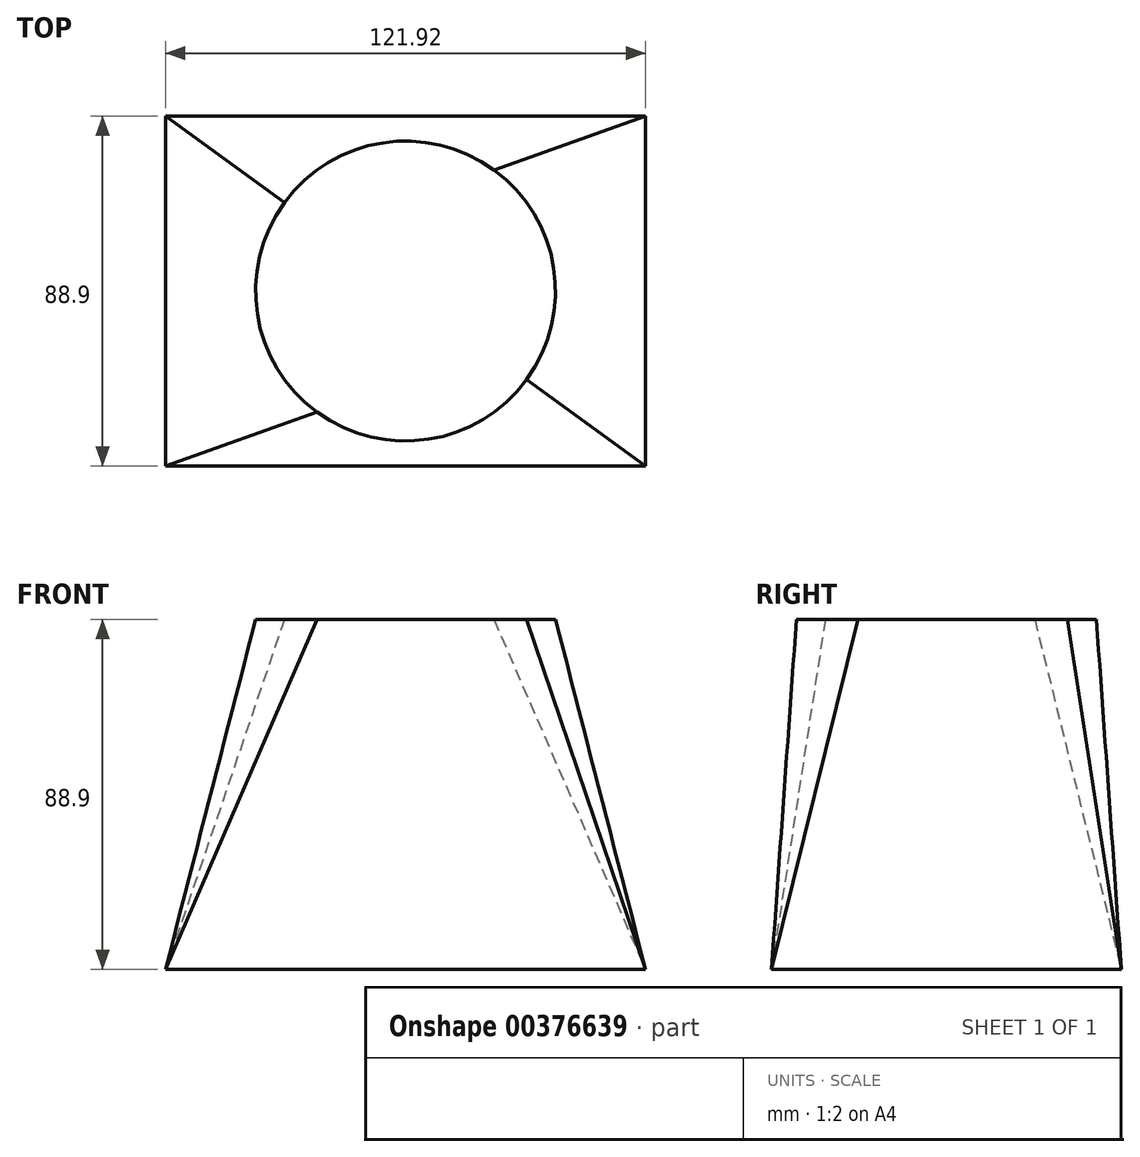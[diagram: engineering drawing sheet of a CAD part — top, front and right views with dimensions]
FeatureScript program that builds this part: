
annotation { "Feature Type Name" : "Feature", "Feature Type Description" : "" }
export const myFeature = defineFeature(function(context is Context, id is Id, definition is map)
    precondition{}
    {
        {
            var Q0;
            Q0=qCreatedBy(makeId("Top.planeOp"),FACE);
            var sketch = newSketch(context, id + "F0", { "sketchPlane" : qUnion([Q0])});
            skLineSegment(sketch, "E0.bottom", {"start": v(-60.96, 44.45) * mm, "end": v(60.96, 44.45) * mm});
            skLineSegment(sketch, "E0.top", {"start": v(-60.96, -44.45) * mm, "end": v(60.96, -44.45) * mm});
            skLineSegment(sketch, "E0.left", {"start": v(-60.96, 44.45) * mm, "end": v(-60.96, -44.45) * mm});
            skLineSegment(sketch, "E0.right", {"start": v(60.96, 44.45) * mm, "end": v(60.96, -44.45) * mm});
            skSolve(sketch);
        }
        {
            var Q0;
            Q0=qCreatedBy(makeId("Top.planeOp"),FACE);
            cPlane(context, id + "F1", {"entities" : qUnion([Q0]), "cplaneType" : CPlaneType.OFFSET, "offset" : 88.9 * mm, "width" : 152.4 * mm, "height" : 152.4 * mm});
        }
        {
            var Q0;
            Q0=qCreatedBy(id+"F1.planeOp",FACE);
            var sketch = newSketch(context, id + "F2", { "sketchPlane" : qUnion([Q0])});
            skCircle(sketch, "E1", {"center": v(0, 0) * mm, "radius": 38.1 * mm});
            skSolve(sketch);
        }
        {
            var Q0;
            Q0=makeQuery(id+"F2.imprint","IMPRINT",FACE,{"disambiguationData":[TD([[makeQuery(id+"F2.imprint","IMPRINT",EDGE,{"derivedFrom":sQuery(id+"F2.wireOp",EDGE,"E1")}),1.0]])]});
            var Q1;
            Q1=makeQuery(id+"F0.imprint","IMPRINT",FACE,{"disambiguationData":[TD([[makeQuery(id+"F0.imprint","IMPRINT",EDGE,{"derivedFrom":sQuery(id+"F0.wireOp",EDGE,"E0.bottom")}),-1.0]])]});
            loft(context, id + "F3", {"sheetProfilesArray" : [{ "sheetProfileEntities" : qUnion([Q0]) }, { "sheetProfileEntities" : qUnion([Q1]) }]});
        }
    });
